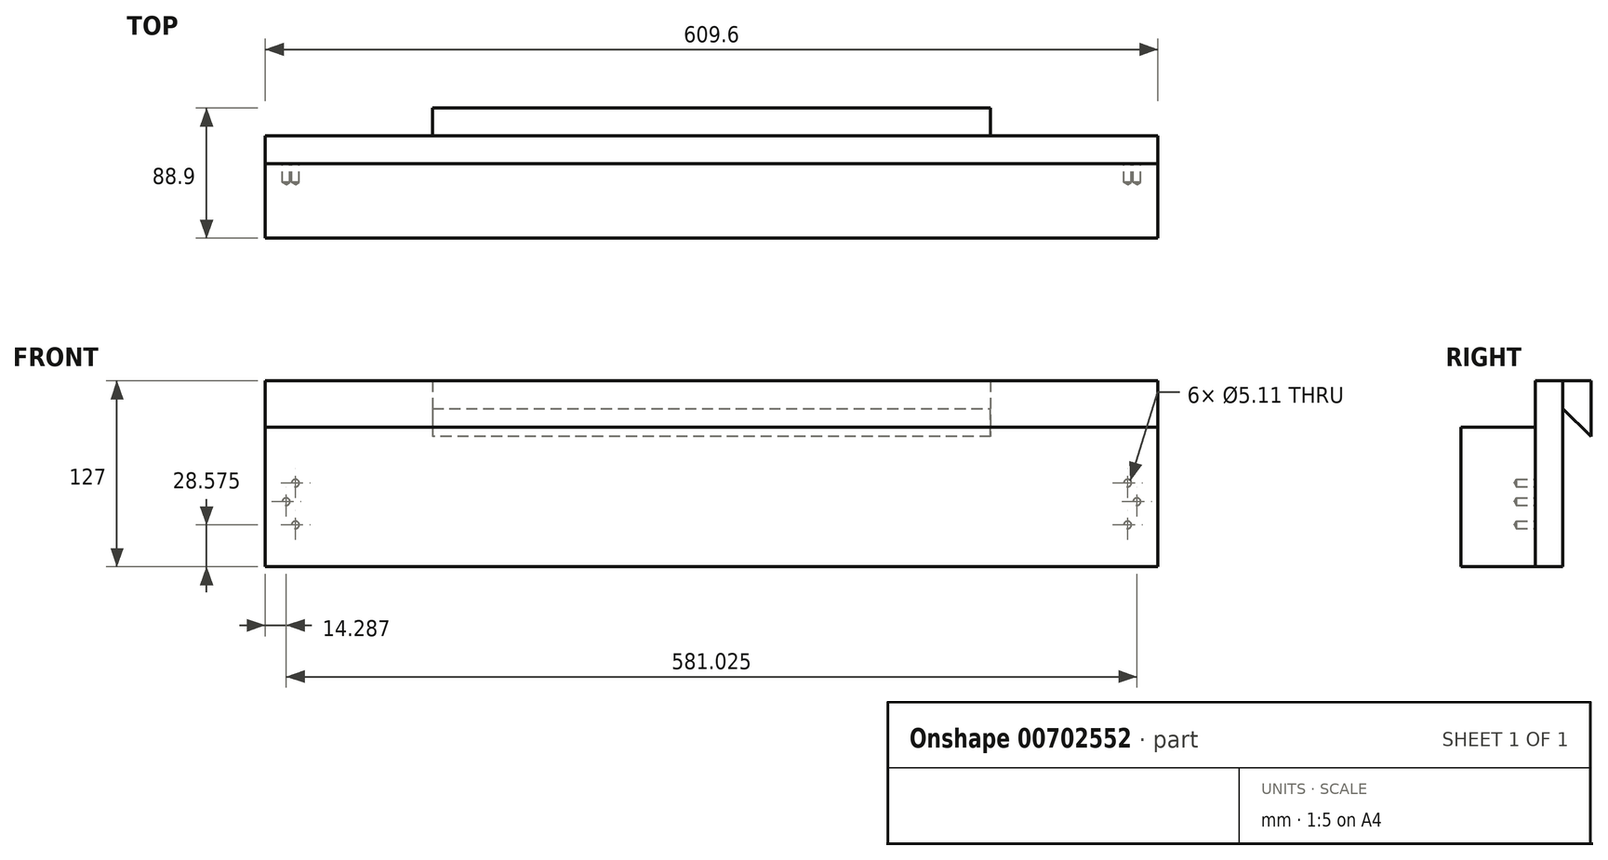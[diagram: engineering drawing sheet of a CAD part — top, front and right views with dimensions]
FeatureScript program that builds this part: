
annotation { "Feature Type Name" : "Feature", "Feature Type Description" : "" }
export const myFeature = defineFeature(function(context is Context, id is Id, definition is map)
    precondition{}
    {
        {
            var Q0;
            Q0=qCreatedBy(makeId("Front.planeOp"),FACE);
            var sketch = newSketch(context, id + "F0", { "sketchPlane" : qUnion([Q0])});
            skLineSegment(sketch, "E0.bottom", {"start": v(0, 0) * mm, "end": v(609.6, 0) * mm});
            skLineSegment(sketch, "E0.top", {"start": v(0, 95.25) * mm, "end": v(609.6, 95.25) * mm});
            skLineSegment(sketch, "E0.left", {"start": v(0, 0) * mm, "end": v(0, 95.25) * mm});
            skLineSegment(sketch, "E0.right", {"start": v(609.6, 0) * mm, "end": v(609.6, 95.25) * mm});
            skSolve(sketch);
        }
        {
            var Q0;
            Q0=makeQuery(id+"F0.imprint","IMPRINT",FACE,{"disambiguationData":[TD([[makeQuery(id+"F0.imprint","IMPRINT",EDGE,{"derivedFrom":sQuery(id+"F0.wireOp",EDGE,"E0.bottom")}),1.0]])]});
            extrude(context, id + "F1", {"entities" : qUnion([Q0]), "depth" : 50.8 * mm, "offsetDistance" : 25.4 * mm});
        }
        {
            var Q0;
            Q0=makeQuery(id+"F1.opExtrude","CAP_FACE",FACE,{"disambiguationData":[OSD([sQuery(id+"F0.wireOp",EDGE,"E0.bottom"),sQuery(id+"F0.wireOp",EDGE,"E0.top"),sQuery(id+"F0.wireOp",EDGE,"E0.left"),sQuery(id+"F0.wireOp",EDGE,"E0.right")])],"isStart":true});
            var sketch = newSketch(context, id + "F2", { "sketchPlane" : qUnion([Q0])});
            skPoint(sketch, "E1", {"position": v(-588.96, 28.58) * mm});
            skPoint(sketch, "E2", {"position": v(-595.31, 44.45) * mm});
            skPoint(sketch, "E3", {"position": v(-588.96, 57.15) * mm});
            skLineSegment(sketch, "E4", {"start": v(-304.8, 95.25) * mm, "end": v(-304.8, 0) * mm, "construction": true});
            skPoint(sketch, "E5.MirrorP", {"position": v(-20.64, 28.58) * mm});
            skPoint(sketch, "E6.MirrorP", {"position": v(-14.29, 44.45) * mm});
            skPoint(sketch, "E7.MirrorP", {"position": v(-20.64, 57.15) * mm});
            skSolve(sketch);
        }
        {
            var Q0;
            Q0=sQuery(id+"F2.wireOp",VERTEX,"E1");
            var Q1;
            Q1=sQuery(id+"F2.wireOp",VERTEX,"E2");
            var Q2;
            Q2=sQuery(id+"F2.wireOp",VERTEX,"E3");
            var Q3;
            Q3=sQuery(id+"F2.wireOp",VERTEX,"E5.MirrorP");
            var Q4;
            Q4=sQuery(id+"F2.wireOp",VERTEX,"E6.MirrorP");
            var Q5;
            Q5=sQuery(id+"F2.wireOp",VERTEX,"E7.MirrorP");
            var Q6;
            Q6=makeQuery(id+"F1.opExtrude","SWEPT_BODY",BODY,{"disambiguationData":[OSD([sQuery(id+"F0.wireOp",EDGE,"E0.bottom"),sQuery(id+"F0.wireOp",EDGE,"E0.top"),sQuery(id+"F0.wireOp",EDGE,"E0.left"),sQuery(id+"F0.wireOp",EDGE,"E0.right")])]});
            hole(context, id + "F3", {"style" : HoleStyle.SIMPLE, "endStyle" : HoleEndStyle.BLIND, "standardTappedOrClearance" : lookupTablePath({ "fit" : "Free", "standard" : "ANSI", "size" : "#10", "type" : "Clearance" }), "standardBlindInLast" : lookupTablePath({ "fit" : "Free", "standard" : "ANSI", "engagement" : "75%", "pitch" : "24 tpi", "size" : "#10", "type" : "Clearance & tapped" }), "holeDiameter" : 5.1 * mm, "majorDiameter" : 6.35 * mm, "holeDepth" : 12.7 * mm, "isTappedThrough" : true, "tappedDepth" : 12.7 * mm, "tapClearance" : 3, "locations" : qUnion([Q0, Q1, Q2, Q3, Q4, Q5]), "scope" : qUnion([Q6])});
        }
        {
            var Q0;
            Q0=makeQuery(id+"F1.opExtrude","CAP_FACE",FACE,{"disambiguationData":[OSD([sQuery(id+"F0.wireOp",EDGE,"E0.bottom"),sQuery(id+"F0.wireOp",EDGE,"E0.top"),sQuery(id+"F0.wireOp",EDGE,"E0.left"),sQuery(id+"F0.wireOp",EDGE,"E0.right")])],"isStart":true});
            var sketch = newSketch(context, id + "F4", { "sketchPlane" : qUnion([Q0])});
            skLineSegment(sketch, "E8.bottom", {"start": v(-609.6, 0) * mm, "end": v(0, 0) * mm});
            skLineSegment(sketch, "E8.top", {"start": v(-609.6, 127) * mm, "end": v(0, 127) * mm});
            skLineSegment(sketch, "E8.left", {"start": v(-609.6, 0) * mm, "end": v(-609.6, 127) * mm});
            skLineSegment(sketch, "E8.right", {"start": v(0, 0) * mm, "end": v(0, 127) * mm});
            skSolve(sketch);
        }
        {
            var Q0;
            Q0 = qSketchRegion(id + "F4", true);
            extrude(context, id + "F5", {"entities" : qUnion([Q0]), "depth" : 19.05 * mm, "offsetDistance" : 25.4 * mm});
        }
        {
            var Q0;
            Q0=makeQuery(id+"F5.opExtrude","CAP_FACE",FACE,{"disambiguationData":[OSD([sQuery(id+"F4.wireOp",EDGE,"E8.bottom"),sQuery(id+"F4.wireOp",EDGE,"E8.top"),sQuery(id+"F4.wireOp",EDGE,"E8.left"),sQuery(id+"F4.wireOp",EDGE,"E8.right")])],"isStart":false});
            var sketch = newSketch(context, id + "F6", { "sketchPlane" : qUnion([Q0])});
            skLineSegment(sketch, "E9", {"start": v(-304.8, 127) * mm, "end": v(-304.8, 0) * mm, "construction": true});
            skLineSegment(sketch, "E10.bottom", {"start": v(-495.3, 127) * mm, "end": v(-114.3, 127) * mm});
            skLineSegment(sketch, "E10.top", {"start": v(-495.3, 88.9) * mm, "end": v(-114.3, 88.9) * mm});
            skLineSegment(sketch, "E10.left", {"start": v(-495.3, 127) * mm, "end": v(-495.3, 88.9) * mm});
            skLineSegment(sketch, "E10.right", {"start": v(-114.3, 127) * mm, "end": v(-114.3, 88.9) * mm});
            skPoint(sketch, "E11", {"position": v(-304.8, 127) * mm});
            skSolve(sketch);
        }
        {
            var Q0;
            Q0 = qSketchRegion(id + "F6", true);
            extrude(context, id + "F7", {"entities" : qUnion([Q0]), "depth" : 19.05 * mm, "offsetDistance" : 25.4 * mm});
        }
        {
            var Q0;
            Q0=makeQuery(id+"F7.opExtrude","SWEPT_FACE",FACE,{"disambiguationData":[OSD([sQuery(id+"F6.wireOp",EDGE,"E10.left")])]});
            var sketch = newSketch(context, id + "F8", { "sketchPlane" : qUnion([Q0])});
            skLineSegment(sketch, "E12", {"start": v(38.1, 88.9) * mm, "end": v(19.05, 107.95) * mm});
            skLineSegment(sketch, "E13", {"start": v(19.05, 107.95) * mm, "end": v(19.05, 88.9) * mm});
            skLineSegment(sketch, "E14", {"start": v(19.05, 88.9) * mm, "end": v(38.1, 88.9) * mm});
            skSolve(sketch);
        }
        {
            var Q0;
            Q0 = qSketchRegion(id + "F8", true);
            extrude(context, id + "F9", {"entities" : qUnion([Q0]), "operationType" : NewBodyOperationType.REMOVE, "endBound" : BoundingType.THROUGH_ALL, "oppositeDirection" : true, "depth" : 25.4 * mm, "offsetDistance" : 25.4 * mm});
        }
    });
